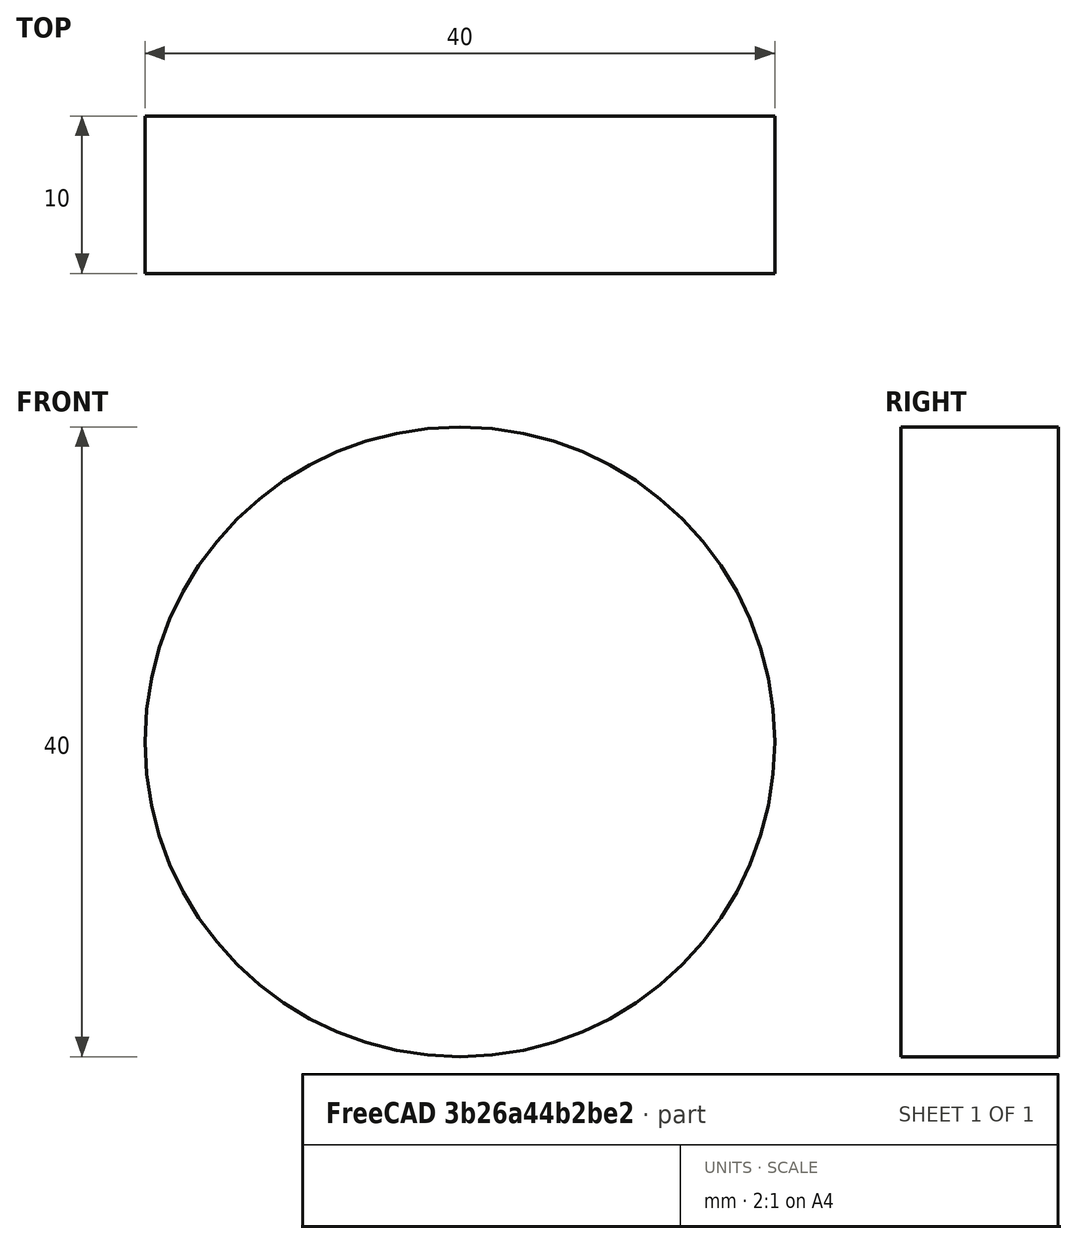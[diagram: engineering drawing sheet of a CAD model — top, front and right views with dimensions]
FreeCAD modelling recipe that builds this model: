
FCSTD DOCUMENT  (FreeCAD 2023.521R14555 (Git shallow))
Label: Circle
License: All rights reserved
objects: Sketcher::SketchObject×1, PartDesign::Pad×1, PartDesign::Body×1, PartDesign::CoordinateSystem×1, App::Part×1, App::Link×1
note: 7 computed .brp shape members not serialized (recipe doc carries the construction recipe); baked Part::Feature solids carry a one-line shape summary decoded from their .brp
EXTERNAL_REF file=Main_board.FCStd obj=Spreadsheet

FEATURE [Sketcher::SketchObject] Sketch
  ArcFitTolerance = 1e-06
  AttachmentSupport = -> [XZ_Plane]
  ExternalBSplineMaxDegree = 5
  ExternalBSplineTolerance = 0.0001
  FullyConstrained = true
  InternalTolerance = 1e-06
  InvalidShape = false
  MakeInternals = false
  MapMode = 5
  Placement = pos=(0,0,0) rot=(1,0,0;1.5708rad)
  Support = -> [XZ_Plane]
  TreeRank = 14
  ValidateShape = false
  expr: Constraints[1] = <<dims>>.PS
  sketch-geometry (1):
    g0: Circle CenterX=0 CenterY=0 CenterZ=0 NormalX=0 NormalY=0 NormalZ=1 AngleXU=0 Radius=20
  constraints (2):
    c: Coincident(g0,g-1)
    c: Diameter(g0) = 40
FEATURE [PartDesign::Pad] Pad
  AddSubType = 0
  AlongSketchNormal = false
  AutoTaperInnerAngle = true
  CheckUpToFaceLimits = true
  ClaimChildren = false
  Direction = (0,-1,-2e-16)
  Fit = 0
  FitJoin = 0
  InnerFit = 0
  InnerFitJoin = 0
  InvalidShape = false
  Length = 10
  Length2 = 10
  Linearize = true
  NewSolid = false
  Profile = -> Sketch
  ReferenceAxis = -> Sketch [N_Axis]
  Suppress = false
  TaperInnerAngle = 0
  TaperInnerAngleRev = 0
  TreeRank = 15
  Type = 0
  ValidateShape = true
  _ProfileBasedVersion = 1
FEATURE [PartDesign::Body] Body
  AutoGroupSolids = false
  ClaimAllChildren = false
  ExportMode = 0
  Group = -> [Sketch,Pad]
  InvalidShape = false
  Origin = -> Origin001
  Tip = -> Pad
  TreeRank = 13
  ValidateShape = false
  _ExportChildren = -> [Pad]
  _GroupVersion = 1
FEATURE [PartDesign::CoordinateSystem] Local_CS
  AttacherType = Attacher::AttachEngine3D
  AttachmentSupport = -> [Pad]
  InvalidShape = false
  MapMode = 5
  Placement = pos=(0,-10,-2.2e-15) rot=(1,0,0;1.5708rad)
  Support = -> [Pad]
  TreeRank = 16
  ValidateShape = false
FEATURE [App::Part] Part  label="Circle"
  ClaimAllChildren = false
  ExportMode = 1
  Group = -> [Body,Local_CS]
  Origin = -> Origin
  TreeRank = 3
  _ExportChildren = -> [Body,Local_CS]
  _GroupVersion = 1
FEATURE [App::Link] Link  label="dims"
  AutoLinkLabel = true
  AutoPlacement = true
  LinkedObject = -> <external Main_board.FCStd>#Spreadsheet
  SyncGroupVisibility = false
  TreeRank = 17
  _LinkVersion = 1

RESOLVED EXTERNAL PARTS (link-assembly join: the EXTERNAL_REF files above that resolve inside this repo's crawl, each included once):
---- part Main_board.FCStd = doc fcstd_18a85a5c1fb4 ----
FCSTD DOCUMENT  (FreeCAD 2023.521R14555 (Git shallow))
Label: Main_board
License: All rights reserved
objects: PartDesign::CoordinateSystem×5, Sketcher::SketchObject×2, PartDesign::Pad×1, Spreadsheet::Sheet×1, PartDesign::Body×1, App::Part×1
note: 13 computed .brp shape members not serialized (recipe doc carries the construction recipe); baked Part::Feature solids carry a one-line shape summary decoded from their .brp

FEATURE [Sketcher::SketchObject] Sketch
  ArcFitTolerance = 1e-06
  AttachmentSupport = -> [XZ_Plane]
  ExternalBSplineMaxDegree = 5
  ExternalBSplineTolerance = 0.0001
  FullyConstrained = true
  InternalTolerance = 1e-06
  InvalidShape = false
  MakeInternals = false
  MapMode = 5
  Placement = pos=(0,0,0) rot=(1,0,0;1.5708rad)
  Support = -> [XZ_Plane]
  TreeRank = 11
  ValidateShape = false
  expr: Constraints[48] = <<dims>>.HS
  sketch-geometry (31):
    g0: LineSegment StartX=-40 StartY=19 StartZ=0 EndX=-21.8135 EndY=50.5 EndZ=0
    g1: LineSegment StartX=-21.8135 StartY=50.5 StartZ=0 EndX=-58.1865 EndY=50.5 EndZ=0
    g2: LineSegment StartX=-58.1865 StartY=50.5 StartZ=0 EndX=-40 EndY=19 EndZ=0
    g3: Circle [constr] CenterX=-40 CenterY=40 CenterZ=0 NormalX=0 NormalY=0 NormalZ=1 AngleXU=0 Radius=21
    g4: LineSegment StartX=40 StartY=-19 StartZ=0 EndX=21.8135 EndY=-50.5 EndZ=0
    g5: LineSegment StartX=21.8135 StartY=-50.5 StartZ=0 EndX=58.1865 EndY=-50.5 EndZ=0
    g6: LineSegment StartX=58.1865 StartY=-50.5 StartZ=0 EndX=40 EndY=-19 EndZ=0
    g7: Circle [constr] CenterX=40 CenterY=-40 CenterZ=0 NormalX=0 NormalY=0 NormalZ=1 AngleXU=0 Radius=21
    g8: LineSegment StartX=27.6565 StartY=23.0106 StartZ=0 EndX=52.3435 EndY=23.0106 EndZ=0
    g9: LineSegment StartX=52.3435 StartY=23.0106 StartZ=0 EndX=59.9722 EndY=46.4894 EndZ=0
    g10: LineSegment StartX=59.9722 StartY=46.4894 StartZ=0 EndX=40 EndY=61 EndZ=0
    g11: LineSegment StartX=40 StartY=61 StartZ=0 EndX=20.0278 EndY=46.4894 EndZ=0
    g12: LineSegment StartX=20.0278 StartY=46.4894 StartZ=0 EndX=27.6565 EndY=23.0106 EndZ=0
    g13: Circle [constr] CenterX=40 CenterY=40 CenterZ=0 NormalX=0 NormalY=0 NormalZ=1 AngleXU=0 Radius=21
    g14: LineSegment StartX=-21.8135 StartY=-29.5 StartZ=0 EndX=-40 EndY=-19 EndZ=0
    g15: LineSegment StartX=-40 StartY=-19 StartZ=0 EndX=-58.1865 EndY=-29.5 EndZ=0
    g16: LineSegment StartX=-58.1865 StartY=-29.5 StartZ=0 EndX=-58.1865 EndY=-50.5 EndZ=0
    g17: LineSegment StartX=-58.1865 StartY=-50.5 StartZ=0 EndX=-40 EndY=-61 EndZ=0
    g18: LineSegment StartX=-40 StartY=-61 StartZ=0 EndX=-21.8135 EndY=-50.5 EndZ=0
    g19: LineSegment StartX=-21.8135 StartY=-50.5 StartZ=0 EndX=-21.8135 EndY=-29.5 EndZ=0
    g20: Circle [constr] CenterX=-40 CenterY=-40 CenterZ=0 NormalX=0 NormalY=0 NormalZ=1 AngleXU=0 Radius=21
    g21: Circle CenterX=0 CenterY=0 CenterZ=0 NormalX=0 NormalY=0 NormalZ=1 AngleXU=0 Radius=21
    g22: LineSegment [constr] StartX=-40 StartY=40 StartZ=0 EndX=40 EndY=40 EndZ=0
    g23: LineSegment [constr] StartX=40 StartY=40 StartZ=0 EndX=40 EndY=-40 EndZ=0
    g24: LineSegment [constr] StartX=40 StartY=-40 StartZ=0 EndX=-40 EndY=-40 EndZ=0
    g25: LineSegment [constr] StartX=-40 StartY=-40 StartZ=0 EndX=-40 EndY=40 EndZ=0
    g26: LineSegment StartX=-70 StartY=-70 StartZ=0 EndX=-70 EndY=70 EndZ=0
    g27: LineSegment StartX=-70 StartY=70 StartZ=0 EndX=70 EndY=70 EndZ=0
    g28: LineSegment StartX=70 StartY=70 StartZ=0 EndX=70 EndY=-70 EndZ=0
    g29: LineSegment StartX=70 StartY=-70 StartZ=0 EndX=-70 EndY=-70 EndZ=0
    g30: GeomPoint [constr] X=0 Y=0 Z=0
  constraints (77):
    c: Coincident(g0,g1)
    c: Coincident(g1,g2)
    c: Coincident(g2,g0)
    c: Equal(g0,g1)
    c: Equal(g0,g2)
    c: PointOnObject(g0,g3)
    c: PointOnObject(g1,g3)
    c: PointOnObject(g2,g3)
    c: Coincident(g4,g5)
    c: Coincident(g5,g6)
    c: Coincident(g6,g4)
    c: Equal(g4,g5)
    c: Equal(g4,g6)
    c: PointOnObject(g4,g7)
    c: PointOnObject(g5,g7)
    c: PointOnObject(g6,g7)
    c: Coincident(g8,g9)
    c: Coincident(g9,g10)
    c: Coincident(g10,g11)
    c: Coincident(g11,g12)
    c: Coincident(g12,g8)
    c: Equal(g8, g9-g12) x4
    c: PointOnObject(g8,g13)
    c: PointOnObject(g9,g13)
    c: PointOnObject(g10,g13)
    c: PointOnObject(g11,g13)
    c: PointOnObject(g12,g13)
    c: Coincident(g14,g15)
    c: Coincident(g15,g16)
    c: Coincident(g16,g17)
    c: Coincident(g17,g18)
    c: Coincident(g18,g19)
    c: Coincident(g19,g14)
    c: Equal(g14, g15-g19) x5
    c: PointOnObject(g14,g20)
    c: PointOnObject(g15,g20)
    c: PointOnObject(g16,g20)
    c: PointOnObject(g17,g20)
    c: PointOnObject(g18,g20)
    c: PointOnObject(g19,g20)
    c: Coincident(g21,g-1)
    c: Diameter(g13) = 42
    c: Horizontal(g8)
    c: Equal(g13,g7)
    c: Equal(g7,g20)
    c: Equal(g20,g3)
    c: Vertical(g19)
    c: Horizontal(g5)
    c: Horizontal(g1)
    c: Coincident(g22,g23)
    c: Coincident(g23,g24)
    c: Coincident(g24,g25)
    c: Coincident(g25,g22)
    c: Horizontal(g22)
    c: Horizontal(g24)
    c: Vertical(g23)
    c: Vertical(g25)
    c: Coincident(g22,g3)
    c: Coincident(g23,g7)
    c: Coincident(g22,g13)
    c: Coincident(g24,g20)
    c: Symmetric(g24,g22,g21)
    c: Equal(g23,g24)
    c: DistanceY(g23,g23) = 80
    c: Coincident(g26,g27)
    c: Coincident(g27,g28)
    c: Coincident(g28,g29)
    c: Coincident(g29,g26)
    c: Horizontal(g27)
    c: Horizontal(g29)
    c: Vertical(g26)
    c: Vertical(g28)
    c: Symmetric(g27,g26,g30)
    c: Coincident(g30,g21)
    c: Equal(g28,g29)
    c: DistanceY(g28,g28) = 140
    c: Equal(g21,g13)
FEATURE [PartDesign::Pad] Pad
  AddSubType = 0
  AlongSketchNormal = false
  AutoTaperInnerAngle = true
  CheckUpToFaceLimits = true
  ClaimChildren = false
  Direction = (0,-1,-2e-16)
  Fit = 0
  FitJoin = 0
  InnerFit = 0
  InnerFitJoin = 0
  InvalidShape = false
  Length = 4
  Length2 = 10
  Linearize = true
  NewSolid = false
  Profile = -> Sketch
  ReferenceAxis = -> Sketch [N_Axis]
  Suppress = false
  TaperInnerAngle = 0
  TaperInnerAngleRev = 0
  TreeRank = 12
  Type = 0
  ValidateShape = true
  _ProfileBasedVersion = 1
FEATURE [PartDesign::CoordinateSystem] Local_CS  label="Triangle0"
  AttacherType = Attacher::AttachEngine3D
  AttachmentSupport = -> [Pad]
  InvalidShape = false
  MapMode = 13
  Placement = pos=(-40,-4,40) rot=(1,0,0;1.5708rad)
  Support = -> [Pad]
  TreeRank = 16
  ValidateShape = false
FEATURE [PartDesign::CoordinateSystem] Local_CS002  label="Triangle1"
  AttacherType = Attacher::AttachEngine3D
  AttachmentOffset = pos=(0,0,0) rot=(0,0,1;3.14159rad)
  AttachmentSupport = -> [Pad]
  InvalidShape = false
  MapMode = 13
  Placement = pos=(40,-4,-40) rot=(0,-0.707107,0.707107;3.14159rad)
  Support = -> [Pad]
  TreeRank = 21
  ValidateShape = false
FEATURE [PartDesign::CoordinateSystem] Local_CS003  label="Circle"
  AttacherType = Attacher::AttachEngine3D
  AttachmentSupport = -> [Pad]
  InvalidShape = false
  MapMode = 11
  Placement = pos=(0,-4,-9e-16) rot=(0.57735,-0.57735,0.57735;2.0944rad)
  Support = -> [Pad]
  TreeRank = 22
  ValidateShape = false
FEATURE [Spreadsheet::Sheet] Spreadsheet  label="dims"
  PythonMode = false
  ShowCells = 0
  TreeRank = 25
  cells = A1=Part SIze; B1(PS)==40mm; A2=Gap; B2==2mm; A3=Hole Size; B3(HS)==B1 + B2
FEATURE [Sketcher::SketchObject] Sketch001
  ArcFitTolerance = 1e-06
  AttachmentSupport = -> [Pad]
  ExternalBSplineMaxDegree = 5
  ExternalBSplineTolerance = 0.0001
  ExternalGeometry = -> [Pad]
  FullyConstrained = true
  InternalTolerance = 1e-06
  InvalidShape = false
  MakeInternals = false
  MapMode = 5
  Placement = pos=(0,-4,-9e-16) rot=(1,0,0;1.5708rad)
  Support = -> [Pad]
  TreeRank = 26
  ValidateShape = false
  sketch-geometry (2):
    g0: Circle CenterX=40 CenterY=40 CenterZ=0 NormalX=0 NormalY=0 NormalZ=1 AngleXU=0 Radius=21
    g1: Circle CenterX=-40 CenterY=-40 CenterZ=0 NormalX=0 NormalY=0 NormalZ=1 AngleXU=0 Radius=21
  constraints (6):
    c: PointOnObject(g-4,g0)
    c: PointOnObject(g-3,g0)
    c: PointOnObject(g-3,g0)
    c: PointOnObject(g-5,g1)
    c: PointOnObject(g-6,g1)
    c: PointOnObject(g-6,g1)
FEATURE [PartDesign::Body] Body
  AutoGroupSolids = false
  ClaimAllChildren = false
  ExportMode = 0
  Group = -> [Sketch,Pad,Sketch001]
  InvalidShape = false
  Origin = -> Origin
  Tip = -> Pad
  TreeRank = 10
  ValidateShape = false
  _ExportChildren = -> [Pad,Sketch001]
  _GroupVersion = 1
FEATURE [PartDesign::CoordinateSystem] Local_CS004  label="Penta"
  AttacherType = Attacher::AttachEngine3D
  AttachmentSupport = -> [Sketch001]
  InvalidShape = false
  MapMode = 11
  Placement = pos=(40,-4,40) rot=(-0.57735,0.57735,-0.57735;4.18879rad)
  Support = -> [Sketch001]
  TreeRank = 23
  ValidateShape = false
FEATURE [PartDesign::CoordinateSystem] Local_CS005  label="Hex"
  AttacherType = Attacher::AttachEngine3D
  AttachmentSupport = -> [Sketch001]
  InvalidShape = false
  MapMode = 11
  Placement = pos=(-40,-4,-40) rot=(-0.57735,0.57735,-0.57735;4.18879rad)
  Support = -> [Sketch001]
  TreeRank = 24
  ValidateShape = false
FEATURE [App::Part] Part
  ClaimAllChildren = false
  ExportMode = 1
  Group = -> [Body,Local_CS,Local_CS002,Local_CS003,Local_CS004,Local_CS005]
  Origin = -> Origin001
  TreeRank = 15
  _ExportChildren = -> [Body,Local_CS,Local_CS002,Local_CS003,Local_CS004,Local_CS005]
  _GroupVersion = 1
